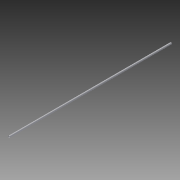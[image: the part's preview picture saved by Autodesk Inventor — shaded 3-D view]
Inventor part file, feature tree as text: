
AUTODESK INVENTOR PART (.ipt)
format: ipt  version: 2014 (Build 180170000, 170)  size: 68,608 bytes
history: native  units: in
note: dims shown in document units (in); Inventor stores cm internally (conversion verified against a paired STEP export)
features: extrude x1, sketch x1
ambient origin geometry x8: Origin, YZ Plane, XZ Plane, XY Plane, X Axis, Y Axis, Z Axis, Center Point
bodies: Solid1 (feature_tree)
feature tree (2):
  extrude  "Extrusion1"  Depth=236.2205in
  sketch  "Sketch1"  dims[d0=2.4803in d1=0.1181in d2=236.2205in d3=0.0in]
